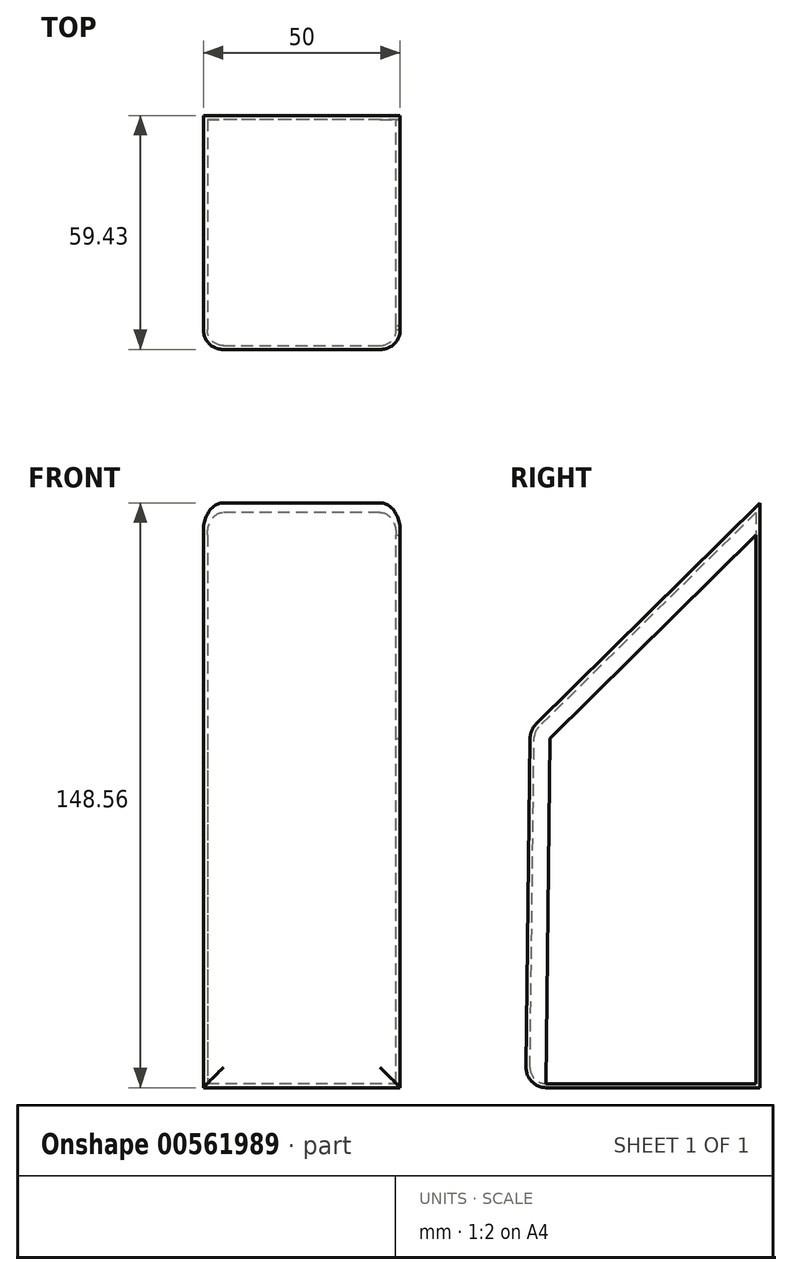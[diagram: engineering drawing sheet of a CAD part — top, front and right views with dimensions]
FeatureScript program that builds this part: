
annotation { "Feature Type Name" : "Feature", "Feature Type Description" : "" }
export const myFeature = defineFeature(function(context is Context, id is Id, definition is map)
    precondition{}
    {
        {
            var Q0;
            Q0=qCreatedBy(makeId("Right.planeOp"),FACE);
            var sketch = newSketch(context, id + "F0", { "sketchPlane" : qUnion([Q0])});
            skLineSegment(sketch, "E0", {"start": v(40.65, 73.17) * mm, "end": v(40.65, -75.39) * mm});
            skLineSegment(sketch, "E1", {"start": v(40.65, -75.39) * mm, "end": v(-18.85, -75.39) * mm});
            skLineSegment(sketch, "E2", {"start": v(-17.74, 15.52) * mm, "end": v(-18.85, -75.39) * mm});
            skLineSegment(sketch, "E3", {"start": v(-17.74, 15.52) * mm, "end": v(40.65, 73.17) * mm});
            skSolve(sketch);
        }
        {
            var Q0;
            Q0 = qSketchRegion(id + "F0", true);
            extrude(context, id + "F1", {"entities" : qUnion([Q0]), "depth" : 50 * mm, "offsetDistance" : 25.4 * mm});
        }
        {
            var Q0;
            Q0=makeQuery(id+"F1.opExtrude","CAP_EDGE",EDGE,{"disambiguationData":[OSD([sQuery(id+"F0.wireOp",EDGE,"E2")])],"isStart":false});
            var Q1;
            Q1=makeQuery(id+"F1.opExtrude","CAP_EDGE",EDGE,{"disambiguationData":[OSD([sQuery(id+"F0.wireOp",EDGE,"E3")])],"isStart":false});
            var Q2;
            Q2=makeQuery(id+"F1.opExtrude","SWEPT_EDGE",EDGE,{"disambiguationData":[OSD([sQuery(id+"F0.wireOp",EDGE,"E2"),sQuery(id+"F0.wireOp",EDGE,"E3")])]});
            var Q3;
            Q3=makeQuery(id+"F1.opExtrude","CAP_EDGE",EDGE,{"disambiguationData":[OSD([sQuery(id+"F0.wireOp",EDGE,"E3")])],"isStart":true});
            var Q4;
            Q4=makeQuery(id+"F1.opExtrude","SWEPT_FACE",FACE,{"disambiguationData":[OSD([sQuery(id+"F0.wireOp",EDGE,"E2")])]});
            fillet(context, id + "F2", {"entities" : qUnion([Q0, Q1, Q2, Q3, Q4]), "radius" : 5.08 * mm, "tangentPropagation" : true, "allowEdgeOverflow" : false});
        }
        {
            var Q0;
            Q0=makeQuery(id+"F1.opExtrude","CAP_FACE",FACE,{"disambiguationData":[OSD([sQuery(id+"F0.wireOp",EDGE,"E0"),sQuery(id+"F0.wireOp",EDGE,"E1"),sQuery(id+"F0.wireOp",EDGE,"E2"),sQuery(id+"F0.wireOp",EDGE,"E3")])],"isStart":false});
            shell(context, id + "F3", {"entities" : qUnion([Q0]), "thickness" : 1 * mm});
        }
    });
